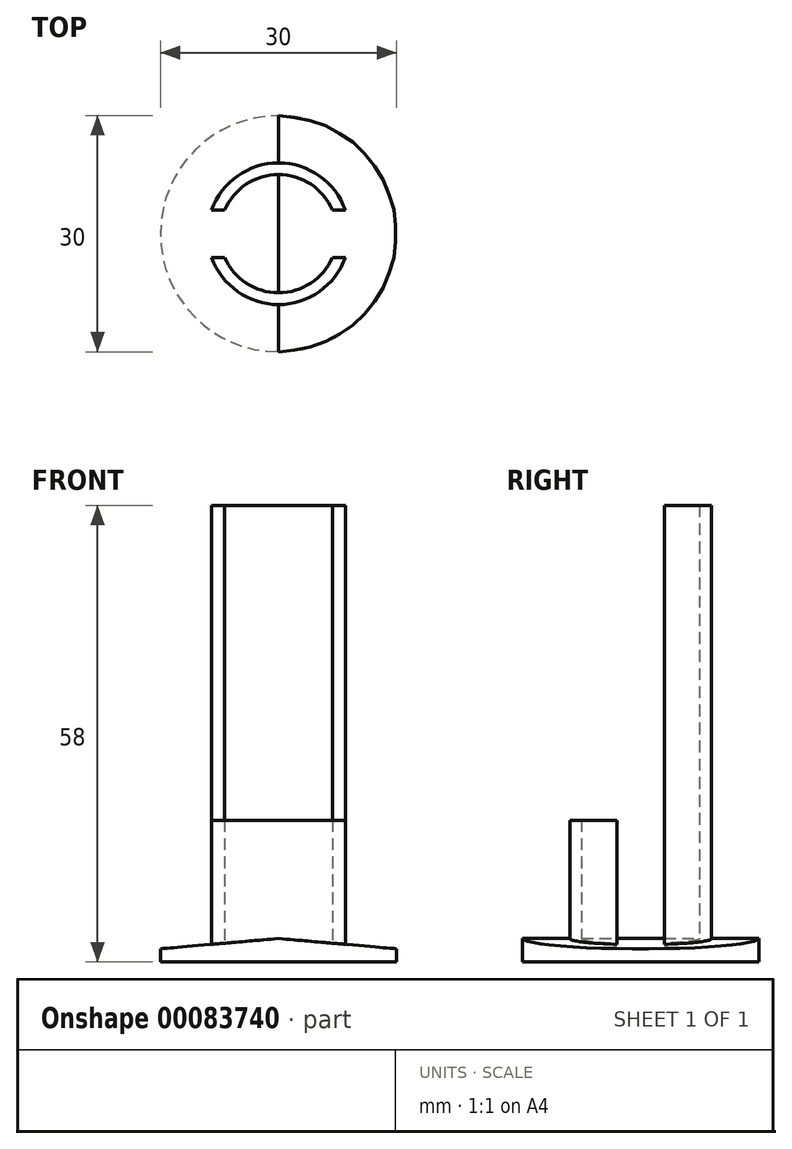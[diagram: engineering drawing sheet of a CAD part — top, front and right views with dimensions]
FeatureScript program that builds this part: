
annotation { "Feature Type Name" : "Feature", "Feature Type Description" : "" }
export const myFeature = defineFeature(function(context is Context, id is Id, definition is map)
    precondition{}
    {
        {
            var Q0;
            Q0=qCreatedBy(makeId("Top.planeOp"),FACE);
            var sketch = newSketch(context, id + "F0", { "sketchPlane" : qUnion([Q0])});
            skCircle(sketch, "E0", {"center": v(0, 0) * mm, "radius": 15 * mm});
            skSolve(sketch);
        }
        {
            var Q0;
            Q0=qSketchRegion(id+"F0",true);
            extrude(context, id + "F1", {"entities" : qUnion([Q0]), "depth" : 3 * mm});
        }
        {
            var Q0;
            Q0=qCreatedBy(makeId("Front.planeOp"),FACE);
            var sketch = newSketch(context, id + "F2", { "sketchPlane" : qUnion([Q0])});
            skLineSegment(sketch, "E1", {"start": v(0, 2.97) * mm, "end": v(-16.28, 1.54) * mm});
            skLineSegment(sketch, "E2", {"start": v(-16.28, 1.54) * mm, "end": v(-16.28, 3.76) * mm});
            skLineSegment(sketch, "E3", {"start": v(-16.28, 3.76) * mm, "end": v(16.03, 3.76) * mm});
            skLineSegment(sketch, "E4", {"start": v(16.03, 3.76) * mm, "end": v(16.03, 1.57) * mm});
            skLineSegment(sketch, "E5", {"start": v(16.03, 1.57) * mm, "end": v(0, 2.97) * mm});
            skSolve(sketch);
        }
        {
            var Q0;
            Q0=qSketchRegion(id+"F2",true);
            extrude(context, id + "F3", {"entities" : qUnion([Q0]), "operationType" : NewBodyOperationType.REMOVE, "endBound" : BoundingType.SYMMETRIC, "depth" : 40 * mm});
        }
        {
            var Q0;
            Q0=qCreatedBy(makeId("Top.planeOp"),FACE);
            var sketch = newSketch(context, id + "F4", { "sketchPlane" : qUnion([Q0])});
            skCircle(sketch, "E6", {"center": v(0, 0) * mm, "radius": 9 * mm});
            skCircle(sketch, "E7", {"center": v(0, 0) * mm, "radius": 7.5 * mm});
            skSolve(sketch);
        }
        {
            var Q0;
            Q0=qSketchRegion(id+"F4",true);
            extrude(context, id + "F5", {"entities" : qUnion([Q0]), "operationType" : NewBodyOperationType.ADD, "depth" : 18 * mm});
        }
        {
            var Q0;
            Q0=qCreatedBy(makeId("Front.planeOp"),FACE);
            var sketch = newSketch(context, id + "F6", { "sketchPlane" : qUnion([Q0])});
            skLineSegment(sketch, "E8", {"start": v(-16.88, 20.5) * mm, "end": v(16.26, 20.5) * mm});
            skLineSegment(sketch, "E9", {"start": v(16.26, 20.5) * mm, "end": v(16.26, 1.55) * mm});
            skLineSegment(sketch, "E10", {"start": v(16.26, 1.55) * mm, "end": v(0, 2.97) * mm});
            skLineSegment(sketch, "E11", {"start": v(0, 2.97) * mm, "end": v(-16.6, 1.52) * mm});
            skLineSegment(sketch, "E12", {"start": v(-16.6, 1.52) * mm, "end": v(-16.88, 20.5) * mm});
            skSolve(sketch);
        }
        {
            var Q0;
            Q0=qSketchRegion(id+"F6",true);
            extrude(context, id + "F7", {"entities" : qUnion([Q0]), "operationType" : NewBodyOperationType.REMOVE, "endBound" : BoundingType.SYMMETRIC, "oppositeDirection" : true, "depth" : 6 * mm});
        }
        {
            var Q0;
            {var subQ0=sQuery(id+"F4.wireOp",EDGE,"E6");var subQ1=sQuery(id+"F4.wireOp",EDGE,"E7");Q0=makeQuery(id+"F7.boolean.opBoolean","SPLIT",FACE,{"disambiguationData":[TD([makeQuery(id+"F7.opExtrude","CAP_FACE",FACE,{"disambiguationData":[OSD([sQuery(id+"F6.wireOp",EDGE,"E8"),sQuery(id+"F6.wireOp",EDGE,"E9"),sQuery(id+"F6.wireOp",EDGE,"E10"),sQuery(id+"F6.wireOp",EDGE,"E11"),sQuery(id+"F6.wireOp",EDGE,"E12")])],"isStart":false})])],"derivedFrom":makeQuery(id+"F5.opExtrude","CAP_FACE",FACE,{"disambiguationData":[OSD([subQ0,subQ1])],"isStart":false})});}
            var sketch = newSketch(context, id + "F8", { "sketchPlane" : qUnion([Q0])});
            skArc(sketch, "E13.0", {"start": v(8.49, 3) * mm, "mid": v(0, 9) * mm, "end": v(-8.49, 3) * mm});
            skLineSegment(sketch, "E13.1", {"start": v(6.87, 3) * mm, "end": v(8.49, 3) * mm});
            skArc(sketch, "E13.2", {"start": v(-6.87, 3) * mm, "mid": v(0, 7.5) * mm, "end": v(6.87, 3) * mm});
            skLineSegment(sketch, "E13.3", {"start": v(-8.49, 3) * mm, "end": v(-6.87, 3) * mm});
            skSolve(sketch);
        }
        {
            var Q0;
            Q0=qSketchRegion(id+"F8",true);
            extrude(context, id + "F9", {"entities" : qUnion([Q0]), "operationType" : NewBodyOperationType.ADD, "depth" : 40 * mm});
        }
    });
